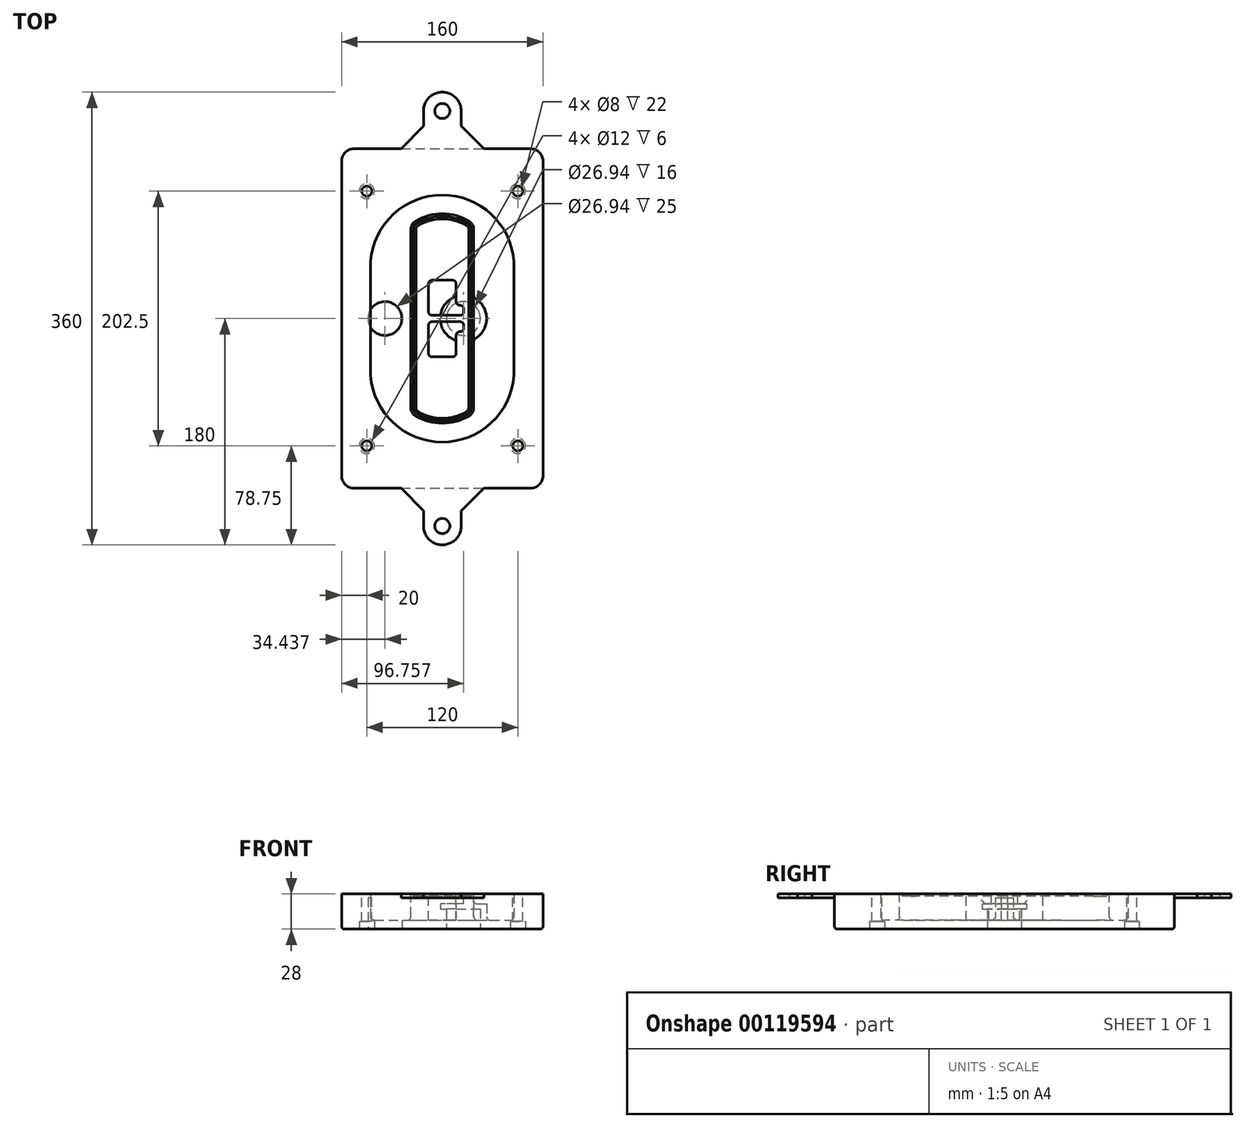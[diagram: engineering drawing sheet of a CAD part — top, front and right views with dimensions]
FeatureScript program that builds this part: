
annotation { "Feature Type Name" : "Feature", "Feature Type Description" : "" }
export const myFeature = defineFeature(function(context is Context, id is Id, definition is map)
    precondition{}
    {
        {
            var Q0;
            Q0=qCreatedBy(makeId("Top.planeOp"),FACE);
            var sketch = newSketch(context, id + "F0", { "sketchPlane" : qUnion([Q0])});
            skPoint(sketch, "E0.rect.middle", {"position": v(0, 0) * mm});
            skLineSegment(sketch, "E1.bottom", {"start": v(-70, -135) * mm, "end": v(70, -135) * mm});
            skLineSegment(sketch, "E1.top", {"start": v(-70, 135) * mm, "end": v(70, 135) * mm});
            skLineSegment(sketch, "E1.left", {"start": v(-80, -125) * mm, "end": v(-80, 125) * mm});
            skLineSegment(sketch, "E1.right", {"start": v(80, -125) * mm, "end": v(80, 125) * mm});
            skLineSegment(sketch, "E2", {"start": v(-80, 135) * mm, "end": v(80, -135) * mm, "construction": true});
            skLineSegment(sketch, "E3", {"start": v(80, 135) * mm, "end": v(-80, -135) * mm, "construction": true});
            skCircle(sketch, "E4", {"center": v(-60, 101.25) * mm, "radius": 4 * mm});
            skCircle(sketch, "E5", {"center": v(60, 101.25) * mm, "radius": 4 * mm});
            skCircle(sketch, "E6", {"center": v(60, -101.25) * mm, "radius": 4 * mm});
            skCircle(sketch, "E7", {"center": v(-60, -101.25) * mm, "radius": 4 * mm});
            skLineSegment(sketch, "E8", {"start": v(-60, 101.25) * mm, "end": v(60, 101.25) * mm, "construction": true});
            skLineSegment(sketch, "E9", {"start": v(60, 101.25) * mm, "end": v(60, -101.25) * mm, "construction": true});
            skLineSegment(sketch, "E10", {"start": v(60, -101.25) * mm, "end": v(-60, -101.25) * mm, "construction": true});
            skLineSegment(sketch, "E11", {"start": v(-60, -101.25) * mm, "end": v(-60, 101.25) * mm, "construction": true});
            skLineSegment(sketch, "E12", {"start": v(-60, 44.66) * mm, "end": v(-60, -44.66) * mm});
            skLineSegment(sketch, "E13", {"start": v(60, 44.66) * mm, "end": v(60, -44.66) * mm});
            skArc(sketch, "E14", {"start": v(59.98, 45.37) * mm, "mid": v(0, 101.25) * mm, "end": v(-59.98, 45.37) * mm});
            skArc(sketch, "E15", {"start": v(-59.98, -45.37) * mm, "mid": v(0, -101.25) * mm, "end": v(59.98, -45.37) * mm});
            skLineSegment(sketch, "E16", {"start": v(-60, 0) * mm, "end": v(60, 0) * mm, "construction": true});
            skPoint(sketch, "E17.visualSharp", {"position": v(-60, -45) * mm});
            skArc(sketch, "E17.filletArc", {"start": v(-60, -44.66) * mm, "mid": v(-60, -45.02) * mm, "end": v(-59.98, -45.37) * mm});
            skPoint(sketch, "E18.visualSharp", {"position": v(-60, 45) * mm});
            skArc(sketch, "E18.filletArc", {"start": v(-59.98, 45.37) * mm, "mid": v(-60, 45.02) * mm, "end": v(-60, 44.66) * mm});
            skPoint(sketch, "E19.visualSharp", {"position": v(60, 45) * mm});
            skArc(sketch, "E19.filletArc", {"start": v(60, 44.66) * mm, "mid": v(60, 45.02) * mm, "end": v(59.98, 45.37) * mm});
            skPoint(sketch, "E20.visualSharp", {"position": v(60, -45) * mm});
            skArc(sketch, "E20.filletArc", {"start": v(59.98, -45.37) * mm, "mid": v(60, -45.02) * mm, "end": v(60, -44.66) * mm});
            skPoint(sketch, "E21.visualSharp", {"position": v(-80, 135) * mm});
            skArc(sketch, "E21.filletArc", {"start": v(-70, 135) * mm, "mid": v(-77.07, 132.07) * mm, "end": v(-80, 125) * mm});
            skPoint(sketch, "E22.visualSharp", {"position": v(80, 135) * mm});
            skArc(sketch, "E22.filletArc", {"start": v(80, 125) * mm, "mid": v(77.07, 132.07) * mm, "end": v(70, 135) * mm});
            skPoint(sketch, "E23.visualSharp", {"position": v(80, -135) * mm});
            skArc(sketch, "E23.filletArc", {"start": v(70, -135) * mm, "mid": v(77.07, -132.07) * mm, "end": v(80, -125) * mm});
            skPoint(sketch, "E24.visualSharp", {"position": v(-80, -135) * mm});
            skArc(sketch, "E24.filletArc", {"start": v(-80, -125) * mm, "mid": v(-77.07, -132.07) * mm, "end": v(-70, -135) * mm});
            skArc(sketch, "E25.0", {"start": v(57, 44.66) * mm, "mid": v(57, 44.9) * mm, "end": v(56.98, 45.16) * mm});
            skLineSegment(sketch, "E25.1", {"start": v(57, 44.66) * mm, "end": v(57, -44.66) * mm});
            skArc(sketch, "E25.2", {"start": v(56.98, -45.16) * mm, "mid": v(57, -44.9) * mm, "end": v(57, -44.66) * mm});
            skArc(sketch, "E25.3", {"start": v(-56.98, -45.16) * mm, "mid": v(0, -98.25) * mm, "end": v(56.98, -45.16) * mm});
            skArc(sketch, "E25.4", {"start": v(-57, -44.66) * mm, "mid": v(-57, -44.9) * mm, "end": v(-56.98, -45.16) * mm});
            skArc(sketch, "E25.5", {"start": v(56.98, 45.16) * mm, "mid": v(0, 98.25) * mm, "end": v(-56.98, 45.16) * mm});
            skLineSegment(sketch, "E25.6", {"start": v(-57, 44.66) * mm, "end": v(-57, -44.66) * mm});
            skArc(sketch, "E25.7", {"start": v(-56.98, 45.16) * mm, "mid": v(-57, 44.9) * mm, "end": v(-57, 44.66) * mm});
            skArc(sketch, "E26.0", {"start": v(-63.97, 45.65) * mm, "mid": v(-64, 45.16) * mm, "end": v(-64, 44.66) * mm});
            skArc(sketch, "E26.1", {"start": v(63.97, 45.65) * mm, "mid": v(0, 105.25) * mm, "end": v(-63.97, 45.65) * mm});
            skArc(sketch, "E26.2", {"start": v(64, 44.66) * mm, "mid": v(64, 45.16) * mm, "end": v(63.97, 45.65) * mm});
            skLineSegment(sketch, "E26.3", {"start": v(64, 44.66) * mm, "end": v(64, -44.66) * mm});
            skArc(sketch, "E26.4", {"start": v(63.97, -45.65) * mm, "mid": v(64, -45.16) * mm, "end": v(64, -44.66) * mm});
            skLineSegment(sketch, "E26.5", {"start": v(-64, 44.66) * mm, "end": v(-64, -44.66) * mm});
            skArc(sketch, "E26.6", {"start": v(-63.97, -45.65) * mm, "mid": v(0, -105.25) * mm, "end": v(63.97, -45.65) * mm});
            skArc(sketch, "E26.7", {"start": v(-64, -44.66) * mm, "mid": v(-64, -45.16) * mm, "end": v(-63.97, -45.65) * mm});
            skSolve(sketch);
        }
        {
            var Q0;
            Q0=makeQuery(id+"F0.imprint","IMPRINT",FACE,{"disambiguationData":[TD([[makeQuery(id+"F0.imprint","IMPRINT",EDGE,{"derivedFrom":sQuery(id+"F0.wireOp",EDGE,"E1.bottom")}),1.0]])]});
            var Q1;
            Q1=makeQuery(id+"F0.imprint","IMPRINT",FACE,{"disambiguationData":[TD([[makeQuery(id+"F0.imprint","IMPRINT",EDGE,{"derivedFrom":sQuery(id+"F0.wireOp",EDGE,"E12")}),1.0]])]});
            var Q2;
            Q2=makeQuery(id+"F0.imprint","IMPRINT",FACE,{"disambiguationData":[TD([[makeQuery(id+"F0.imprint","IMPRINT",EDGE,{"derivedFrom":sQuery(id+"F0.wireOp",EDGE,"E25.0")}),1.0]])]});
            var Q3;
            Q3=makeQuery(id+"F0.imprint","IMPRINT",FACE,{"disambiguationData":[TD([[makeQuery(id+"F0.imprint","IMPRINT",EDGE,{"derivedFrom":sQuery(id+"F0.wireOp",EDGE,"E12")}),-1.0]])]});
            extrude(context, id + "F1", {"entities" : qUnion([Q0, Q1, Q2, Q3]), "oppositeDirection" : true, "depth" : 25 * mm});
        }
        {
            var Q0;
            Q0=makeQuery(id+"F0.imprint","IMPRINT",FACE,{"disambiguationData":[TD([[makeQuery(id+"F0.imprint","IMPRINT",EDGE,{"derivedFrom":sQuery(id+"F0.wireOp",EDGE,"E12")}),1.0]])]});
            extrude(context, id + "F2", {"entities" : qUnion([Q0]), "operationType" : NewBodyOperationType.ADD, "depth" : 3 * mm});
        }
        {
            var Q0;
            Q0=makeQuery(id+"F0.imprint","IMPRINT",FACE,{"disambiguationData":[TD([[makeQuery(id+"F0.imprint","IMPRINT",EDGE,{"derivedFrom":sQuery(id+"F0.wireOp",EDGE,"E25.0")}),1.0]])]});
            extrude(context, id + "F3", {"entities" : qUnion([Q0]), "operationType" : NewBodyOperationType.REMOVE, "oppositeDirection" : true, "depth" : 18 * mm});
        }
        {
            var Q0;
            Q0=makeQuery(id+"F2.opExtrude","CAP_FACE",FACE,{"disambiguationData":[OSD([sQuery(id+"F0.wireOp",EDGE,"E12"),sQuery(id+"F0.wireOp",EDGE,"E13"),sQuery(id+"F0.wireOp",EDGE,"E14"),sQuery(id+"F0.wireOp",EDGE,"E15"),sQuery(id+"F0.wireOp",EDGE,"E17.filletArc"),sQuery(id+"F0.wireOp",EDGE,"E18.filletArc"),sQuery(id+"F0.wireOp",EDGE,"E19.filletArc"),sQuery(id+"F0.wireOp",EDGE,"E20.filletArc"),sQuery(id+"F0.wireOp",EDGE,"E25.0"),sQuery(id+"F0.wireOp",EDGE,"E25.1"),sQuery(id+"F0.wireOp",EDGE,"E25.2"),sQuery(id+"F0.wireOp",EDGE,"E25.3"),sQuery(id+"F0.wireOp",EDGE,"E25.4"),sQuery(id+"F0.wireOp",EDGE,"E25.5"),sQuery(id+"F0.wireOp",EDGE,"E25.6"),sQuery(id+"F0.wireOp",EDGE,"E25.7")])],"isStart":false});
            var sketch = newSketch(context, id + "F4", { "sketchPlane" : qUnion([Q0])});
            skArc(sketch, "E27.0", {"start": v(-20.99, -77.65) * mm, "mid": v(0, -83.25) * mm, "end": v(20.99, -77.65) * mm});
            skArc(sketch, "E28.0", {"start": v(20.99, 77.65) * mm, "mid": v(0, 83.25) * mm, "end": v(-20.99, 77.65) * mm});
            skLineSegment(sketch, "E29", {"start": v(-25, 70.71) * mm, "end": v(-25, -70.71) * mm});
            skLineSegment(sketch, "E30", {"start": v(25, 70.71) * mm, "end": v(25, -70.71) * mm});
            skLineSegment(sketch, "E31", {"start": v(-25, 75.03) * mm, "end": v(25, 75.03) * mm, "construction": true});
            skLineSegment(sketch, "E32", {"start": v(-25, -75.03) * mm, "end": v(25, -75.03) * mm, "construction": true});
            skPoint(sketch, "E33.visualSharp", {"position": v(-25, 75.03) * mm});
            skArc(sketch, "E33.filletArc", {"start": v(-20.99, 77.65) * mm, "mid": v(-23.92, 74.72) * mm, "end": v(-25, 70.71) * mm});
            skPoint(sketch, "E34.visualSharp", {"position": v(25, 75.03) * mm});
            skArc(sketch, "E34.filletArc", {"start": v(25, 70.71) * mm, "mid": v(23.92, 74.72) * mm, "end": v(20.99, 77.65) * mm});
            skPoint(sketch, "E35.visualSharp", {"position": v(25, -75.03) * mm});
            skArc(sketch, "E35.filletArc", {"start": v(20.99, -77.65) * mm, "mid": v(23.92, -74.72) * mm, "end": v(25, -70.71) * mm});
            skPoint(sketch, "E36.visualSharp", {"position": v(-25, -75.03) * mm});
            skArc(sketch, "E36.filletArc", {"start": v(-25, -70.71) * mm, "mid": v(-23.92, -74.72) * mm, "end": v(-20.99, -77.65) * mm});
            skArc(sketch, "E37.0", {"start": v(56.98, 45.16) * mm, "mid": v(0, 98.25) * mm, "end": v(-56.98, 45.16) * mm});
            skArc(sketch, "E37.1", {"start": v(-56.98, 45.16) * mm, "mid": v(-57, 44.9) * mm, "end": v(-57, 44.66) * mm});
            skLineSegment(sketch, "E37.2", {"start": v(-57, 44.66) * mm, "end": v(-57, -44.66) * mm});
            skArc(sketch, "E37.3", {"start": v(-57, -44.66) * mm, "mid": v(-57, -44.9) * mm, "end": v(-56.98, -45.16) * mm});
            skArc(sketch, "E37.4", {"start": v(-56.98, -45.16) * mm, "mid": v(0, -98.25) * mm, "end": v(56.98, -45.16) * mm});
            skArc(sketch, "E37.5", {"start": v(56.98, -45.16) * mm, "mid": v(57, -44.9) * mm, "end": v(57, -44.66) * mm});
            skLineSegment(sketch, "E37.6", {"start": v(57, 44.66) * mm, "end": v(57, -44.66) * mm});
            skArc(sketch, "E37.7", {"start": v(57, 44.66) * mm, "mid": v(57, 44.9) * mm, "end": v(56.98, 45.16) * mm});
            skLineSegment(sketch, "E38.0", {"start": v(23, 70.71) * mm, "end": v(23, -70.71) * mm});
            skArc(sketch, "E38.1", {"start": v(19.99, -75.92) * mm, "mid": v(22.2, -73.72) * mm, "end": v(23, -70.71) * mm});
            skArc(sketch, "E38.2", {"start": v(-19.99, -75.92) * mm, "mid": v(0, -81.25) * mm, "end": v(19.99, -75.92) * mm});
            skArc(sketch, "E38.3", {"start": v(-23, -70.71) * mm, "mid": v(-22.2, -73.72) * mm, "end": v(-19.99, -75.92) * mm});
            skLineSegment(sketch, "E38.4", {"start": v(-23, 70.71) * mm, "end": v(-23, -70.71) * mm});
            skArc(sketch, "E38.5", {"start": v(23, 70.71) * mm, "mid": v(22.2, 73.72) * mm, "end": v(19.99, 75.92) * mm});
            skArc(sketch, "E38.6", {"start": v(-19.99, 75.92) * mm, "mid": v(-22.2, 73.72) * mm, "end": v(-23, 70.71) * mm});
            skArc(sketch, "E38.7", {"start": v(19.99, 75.92) * mm, "mid": v(0, 81.25) * mm, "end": v(-19.99, 75.92) * mm});
            skArc(sketch, "E39.0", {"start": v(21, 70.71) * mm, "mid": v(20.46, 72.72) * mm, "end": v(19, 74.18) * mm});
            skLineSegment(sketch, "E39.1", {"start": v(21, 70.71) * mm, "end": v(21, -70.71) * mm});
            skArc(sketch, "E39.2", {"start": v(19, -74.18) * mm, "mid": v(20.46, -72.72) * mm, "end": v(21, -70.71) * mm});
            skArc(sketch, "E39.3", {"start": v(-19, -74.18) * mm, "mid": v(0, -79.25) * mm, "end": v(19, -74.18) * mm});
            skArc(sketch, "E39.4", {"start": v(-21, -70.71) * mm, "mid": v(-20.46, -72.72) * mm, "end": v(-19, -74.18) * mm});
            skArc(sketch, "E39.5", {"start": v(19, 74.18) * mm, "mid": v(0, 79.25) * mm, "end": v(-19, 74.18) * mm});
            skLineSegment(sketch, "E39.6", {"start": v(-21, 70.71) * mm, "end": v(-21, -70.71) * mm});
            skArc(sketch, "E39.7", {"start": v(-19, 74.18) * mm, "mid": v(-20.46, 72.72) * mm, "end": v(-21, 70.71) * mm});
            skLineSegment(sketch, "E40", {"start": v(-25, 0) * mm, "end": v(25, 0) * mm, "construction": true});
            skLineSegment(sketch, "E41", {"start": v(-11, 5.5) * mm, "end": v(-11, 27.5) * mm});
            skLineSegment(sketch, "E42", {"start": v(-8, 30.5) * mm, "end": v(8, 30.5) * mm});
            skLineSegment(sketch, "E43", {"start": v(11, 27.5) * mm, "end": v(11, 13.5) * mm});
            skLineSegment(sketch, "E44", {"start": v(14, 10.5) * mm, "end": v(14, 10.5) * mm});
            skLineSegment(sketch, "E45", {"start": v(17, 7.5) * mm, "end": v(17, 5.5) * mm});
            skLineSegment(sketch, "E46", {"start": v(14, 2.5) * mm, "end": v(-8, 2.5) * mm});
            skPoint(sketch, "E47.visualSharp", {"position": v(-11, 30.5) * mm});
            skArc(sketch, "E47.filletArc", {"start": v(-8, 30.5) * mm, "mid": v(-10.12, 29.62) * mm, "end": v(-11, 27.5) * mm});
            skPoint(sketch, "E48.visualSharp", {"position": v(11, 30.5) * mm});
            skArc(sketch, "E48.filletArc", {"start": v(11, 27.5) * mm, "mid": v(10.12, 29.62) * mm, "end": v(8, 30.5) * mm});
            skPoint(sketch, "E49.visualSharp", {"position": v(11, 10.5) * mm});
            skArc(sketch, "E49.filletArc", {"start": v(11, 13.5) * mm, "mid": v(11.88, 11.38) * mm, "end": v(14, 10.5) * mm});
            skPoint(sketch, "E50.visualSharp", {"position": v(17, 10.5) * mm});
            skArc(sketch, "E50.filletArc", {"start": v(17, 7.5) * mm, "mid": v(16.12, 9.62) * mm, "end": v(14, 10.5) * mm});
            skPoint(sketch, "E51.visualSharp", {"position": v(17, 2.5) * mm});
            skArc(sketch, "E51.filletArc", {"start": v(14, 2.5) * mm, "mid": v(16.12, 3.38) * mm, "end": v(17, 5.5) * mm});
            skPoint(sketch, "E52.visualSharp", {"position": v(-11, 2.5) * mm});
            skArc(sketch, "E52.filletArc", {"start": v(-11, 5.5) * mm, "mid": v(-10.12, 3.38) * mm, "end": v(-8, 2.5) * mm});
            skLineSegment(sketch, "E53.0.MirrorCS", {"start": v(14, -2.5) * mm, "end": v(-8, -2.5) * mm});
            skArc(sketch, "E54.0.MirrorCS", {"start": v(-11, -5.5) * mm, "mid": v(-10.12, -3.38) * mm, "end": v(-8, -2.5) * mm});
            skLineSegment(sketch, "E55.0.MirrorCS", {"start": v(-11, -5.5) * mm, "end": v(-11, -27.5) * mm});
            skArc(sketch, "E56.0.MirrorCS", {"start": v(-8, -30.5) * mm, "mid": v(-10.12, -29.62) * mm, "end": v(-11, -27.5) * mm});
            skLineSegment(sketch, "E57.0.MirrorCS", {"start": v(-8, -30.5) * mm, "end": v(8, -30.5) * mm});
            skArc(sketch, "E58.0.MirrorCS", {"start": v(11, -27.5) * mm, "mid": v(10.12, -29.62) * mm, "end": v(8, -30.5) * mm});
            skLineSegment(sketch, "E59.0.MirrorCS", {"start": v(11, -27.5) * mm, "end": v(11, -13.5) * mm});
            skArc(sketch, "E60.0.MirrorCS", {"start": v(11, -13.5) * mm, "mid": v(11.88, -11.38) * mm, "end": v(14, -10.5) * mm});
            skArc(sketch, "E61.0.MirrorCS", {"start": v(17, -7.5) * mm, "mid": v(16.12, -9.62) * mm, "end": v(14, -10.5) * mm});
            skLineSegment(sketch, "E62.0.MirrorCS", {"start": v(17, -7.5) * mm, "end": v(17, -5.5) * mm});
            skArc(sketch, "E63.0.MirrorCS", {"start": v(14, -2.5) * mm, "mid": v(16.12, -3.38) * mm, "end": v(17, -5.5) * mm});
            skSolve(sketch);
        }
        {
            var Q0;
            Q0=makeQuery(id+"F4.imprint","IMPRINT",FACE,{"disambiguationData":[TD([[makeQuery(id+"F4.imprint","IMPRINT",EDGE,{"derivedFrom":sQuery(id+"F4.wireOp",EDGE,"E27.0")}),1.0]])]});
            var Q1;
            Q1=makeQuery(id+"F4.imprint","IMPRINT",FACE,{"disambiguationData":[TD([[makeQuery(id+"F4.imprint","IMPRINT",EDGE,{"derivedFrom":sQuery(id+"F4.wireOp",EDGE,"E38.0")}),-1.0]])]});
            var Q2;
            Q2=makeQuery(id+"F4.imprint","IMPRINT",FACE,{"disambiguationData":[TD([[makeQuery(id+"F4.imprint","IMPRINT",EDGE,{"derivedFrom":sQuery(id+"F4.wireOp",EDGE,"E39.0")}),1.0]])]});
            extrude(context, id + "F5", {"entities" : qUnion([Q0, Q1, Q2]), "operationType" : NewBodyOperationType.ADD, "endBound" : BoundingType.UP_TO_NEXT, "oppositeDirection" : true, "depth" : 25 * mm});
        }
        {
            var Q0;
            Q0=makeQuery(id+"F4.imprint","IMPRINT",FACE,{"disambiguationData":[TD([[makeQuery(id+"F4.imprint","IMPRINT",EDGE,{"derivedFrom":sQuery(id+"F4.wireOp",EDGE,"E38.0")}),-1.0]])]});
            extrude(context, id + "F6", {"entities" : qUnion([Q0]), "operationType" : NewBodyOperationType.REMOVE, "oppositeDirection" : true, "depth" : 2 * mm});
        }
        {
            var Q0;
            Q0=makeQuery(id+"F1.opExtrude","CAP_FACE",FACE,{"disambiguationData":[OSD([sQuery(id+"F0.wireOp",EDGE,"E1.bottom"),sQuery(id+"F0.wireOp",EDGE,"E1.top"),sQuery(id+"F0.wireOp",EDGE,"E1.left"),sQuery(id+"F0.wireOp",EDGE,"E1.right"),sQuery(id+"F0.wireOp",EDGE,"E4"),sQuery(id+"F0.wireOp",EDGE,"E5"),sQuery(id+"F0.wireOp",EDGE,"E6"),sQuery(id+"F0.wireOp",EDGE,"E7"),sQuery(id+"F0.wireOp",EDGE,"E21.filletArc"),sQuery(id+"F0.wireOp",EDGE,"E22.filletArc"),sQuery(id+"F0.wireOp",EDGE,"E23.filletArc"),sQuery(id+"F0.wireOp",EDGE,"E24.filletArc")])],"isStart":false});
            var sketch = newSketch(context, id + "F7", { "sketchPlane" : qUnion([Q0])});
            skCircle(sketch, "E64", {"center": v(16.76, 0) * mm, "radius": 13.47 * mm});
            skCircle(sketch, "E65", {"center": v(-45.56, 0) * mm, "radius": 13.47 * mm});
            skLineSegment(sketch, "E66", {"start": v(80, 0) * mm, "end": v(-80, 0) * mm});
            skCircle(sketch, "E67", {"center": v(16.76, 0) * mm, "radius": 18.47 * mm});
            skCircle(sketch, "E68", {"center": v(60, -101.25) * mm, "radius": 6 * mm});
            skCircle(sketch, "E69", {"center": v(-60, -101.25) * mm, "radius": 6 * mm});
            skCircle(sketch, "E70", {"center": v(-60, 101.25) * mm, "radius": 6 * mm});
            skCircle(sketch, "E71", {"center": v(60, 101.25) * mm, "radius": 6 * mm});
            skSolve(sketch);
        }
        {
            var Q0;
            {var subQ1=sQuery(id+"F7.wireOp",EDGE,"E66");var subQ4=sQuery(id+"F7.wireOp",EDGE,"E64");var subQ6=makeQuery(id+"F7.imprint","INTERSECT",VERTEX,{"disambiguationData":[OD(0.0)],"derivedFrom":[subQ4,subQ1]});Q0=makeQuery(id+"F7.imprint","IMPRINT",FACE,{"disambiguationData":[TD([[makeQuery(id+"F7.imprint","IMPRINT",EDGE,{"disambiguationData":[TD([[subQ6,-1.0]])],"derivedFrom":subQ4}),-1.0]])]});}
            var Q1;
            {var subQ0=sQuery(id+"F7.wireOp",EDGE,"E66");var subQ1=sQuery(id+"F7.wireOp",EDGE,"E64");var subQ3=makeQuery(id+"F7.imprint","INTERSECT",VERTEX,{"disambiguationData":[OD(0.0)],"derivedFrom":[subQ1,subQ0]});Q1=makeQuery(id+"F7.imprint","IMPRINT",FACE,{"disambiguationData":[TD([[makeQuery(id+"F7.imprint","IMPRINT",EDGE,{"disambiguationData":[TD([[subQ3,-1.0]])],"derivedFrom":subQ1}),1.0]])]});}
            var Q2;
            {var subQ0=sQuery(id+"F7.wireOp",EDGE,"E66");var subQ1=sQuery(id+"F7.wireOp",EDGE,"E64");var subQ3=makeQuery(id+"F7.imprint","INTERSECT",VERTEX,{"disambiguationData":[OD(0.0)],"derivedFrom":[subQ1,subQ0]});Q2=makeQuery(id+"F7.imprint","IMPRINT",FACE,{"disambiguationData":[TD([[makeQuery(id+"F7.imprint","IMPRINT",EDGE,{"disambiguationData":[TD([[subQ3,1.0]])],"derivedFrom":subQ1}),1.0]])]});}
            var Q3;
            {var subQ1=sQuery(id+"F7.wireOp",EDGE,"E66");var subQ4=sQuery(id+"F7.wireOp",EDGE,"E64");var subQ6=makeQuery(id+"F7.imprint","INTERSECT",VERTEX,{"disambiguationData":[OD(0.0)],"derivedFrom":[subQ4,subQ1]});Q3=makeQuery(id+"F7.imprint","IMPRINT",FACE,{"disambiguationData":[TD([[makeQuery(id+"F7.imprint","IMPRINT",EDGE,{"disambiguationData":[TD([[subQ6,1.0]])],"derivedFrom":subQ4}),-1.0]])]});}
            extrude(context, id + "F8", {"entities" : qUnion([Q0, Q1, Q2, Q3]), "operationType" : NewBodyOperationType.ADD, "oppositeDirection" : true, "depth" : 20 * mm});
        }
        {
            var Q0;
            {var subQ0=sQuery(id+"F7.wireOp",EDGE,"E66");var subQ1=sQuery(id+"F7.wireOp",EDGE,"E64");var subQ3=makeQuery(id+"F7.imprint","INTERSECT",VERTEX,{"disambiguationData":[OD(0.0)],"derivedFrom":[subQ1,subQ0]});Q0=makeQuery(id+"F7.imprint","IMPRINT",FACE,{"disambiguationData":[TD([[makeQuery(id+"F7.imprint","IMPRINT",EDGE,{"disambiguationData":[TD([[subQ3,-1.0]])],"derivedFrom":subQ1}),1.0]])]});}
            var Q1;
            {var subQ0=sQuery(id+"F7.wireOp",EDGE,"E66");var subQ1=sQuery(id+"F7.wireOp",EDGE,"E64");var subQ3=makeQuery(id+"F7.imprint","INTERSECT",VERTEX,{"disambiguationData":[OD(0.0)],"derivedFrom":[subQ1,subQ0]});Q1=makeQuery(id+"F7.imprint","IMPRINT",FACE,{"disambiguationData":[TD([[makeQuery(id+"F7.imprint","IMPRINT",EDGE,{"disambiguationData":[TD([[subQ3,1.0]])],"derivedFrom":subQ1}),1.0]])]});}
            extrude(context, id + "F9", {"entities" : qUnion([Q0, Q1]), "operationType" : NewBodyOperationType.REMOVE, "oppositeDirection" : true, "depth" : 16 * mm});
        }
        {
            var Q0;
            {var subQ0=sQuery(id+"F7.wireOp",EDGE,"E66");var subQ1=sQuery(id+"F7.wireOp",EDGE,"E65");var subQ3=makeQuery(id+"F7.imprint","INTERSECT",VERTEX,{"disambiguationData":[OD(0.0)],"derivedFrom":[subQ1,subQ0]});Q0=makeQuery(id+"F7.imprint","IMPRINT",FACE,{"disambiguationData":[TD([[makeQuery(id+"F7.imprint","IMPRINT",EDGE,{"disambiguationData":[TD([[subQ3,-1.0]])],"derivedFrom":subQ1}),1.0]])]});}
            var Q1;
            {var subQ0=sQuery(id+"F7.wireOp",EDGE,"E66");var subQ1=sQuery(id+"F7.wireOp",EDGE,"E65");var subQ3=makeQuery(id+"F7.imprint","INTERSECT",VERTEX,{"disambiguationData":[OD(0.0)],"derivedFrom":[subQ1,subQ0]});Q1=makeQuery(id+"F7.imprint","IMPRINT",FACE,{"disambiguationData":[TD([[makeQuery(id+"F7.imprint","IMPRINT",EDGE,{"disambiguationData":[TD([[subQ3,1.0]])],"derivedFrom":subQ1}),1.0]])]});}
            extrude(context, id + "F10", {"entities" : qUnion([Q0, Q1]), "operationType" : NewBodyOperationType.REMOVE, "oppositeDirection" : true, "depth" : 25 * mm});
        }
        {
            var Q0;
            Q0=makeQuery(id+"F7.imprint","IMPRINT",FACE,{"disambiguationData":[TD([[makeQuery(id+"F7.imprint","IMPRINT",EDGE,{"derivedFrom":sQuery(id+"F7.wireOp",EDGE,"E68")}),1.0]])]});
            var Q1;
            Q1=makeQuery(id+"F7.imprint","IMPRINT",FACE,{"disambiguationData":[TD([[makeQuery(id+"F7.imprint","IMPRINT",EDGE,{"derivedFrom":makeQuery(id+"F1.opExtrude","CAP_EDGE",EDGE,{"disambiguationData":[OSD([sQuery(id+"F0.wireOp",EDGE,"E5")])],"isStart":false})}),-1.0]])]});
            var Q2;
            Q2=makeQuery(id+"F7.imprint","IMPRINT",FACE,{"disambiguationData":[TD([[makeQuery(id+"F7.imprint","IMPRINT",EDGE,{"derivedFrom":sQuery(id+"F7.wireOp",EDGE,"E69")}),1.0]])]});
            var Q3;
            Q3=makeQuery(id+"F7.imprint","IMPRINT",FACE,{"disambiguationData":[TD([[makeQuery(id+"F7.imprint","IMPRINT",EDGE,{"derivedFrom":makeQuery(id+"F1.opExtrude","CAP_EDGE",EDGE,{"disambiguationData":[OSD([sQuery(id+"F0.wireOp",EDGE,"E4")])],"isStart":false})}),-1.0]])]});
            var Q4;
            Q4=makeQuery(id+"F7.imprint","IMPRINT",FACE,{"disambiguationData":[TD([[makeQuery(id+"F7.imprint","IMPRINT",EDGE,{"derivedFrom":sQuery(id+"F7.wireOp",EDGE,"E70")}),1.0]])]});
            var Q5;
            Q5=makeQuery(id+"F7.imprint","IMPRINT",FACE,{"disambiguationData":[TD([[makeQuery(id+"F7.imprint","IMPRINT",EDGE,{"derivedFrom":makeQuery(id+"F1.opExtrude","CAP_EDGE",EDGE,{"disambiguationData":[OSD([sQuery(id+"F0.wireOp",EDGE,"E7")])],"isStart":false})}),-1.0]])]});
            var Q6;
            Q6=makeQuery(id+"F7.imprint","IMPRINT",FACE,{"disambiguationData":[TD([[makeQuery(id+"F7.imprint","IMPRINT",EDGE,{"derivedFrom":sQuery(id+"F7.wireOp",EDGE,"E71")}),1.0]])]});
            var Q7;
            Q7=makeQuery(id+"F7.imprint","IMPRINT",FACE,{"disambiguationData":[TD([[makeQuery(id+"F7.imprint","IMPRINT",EDGE,{"derivedFrom":makeQuery(id+"F1.opExtrude","CAP_EDGE",EDGE,{"disambiguationData":[OSD([sQuery(id+"F0.wireOp",EDGE,"E6")])],"isStart":false})}),-1.0]])]});
            extrude(context, id + "F11", {"entities" : qUnion([Q0, Q1, Q2, Q3, Q4, Q5, Q6, Q7]), "operationType" : NewBodyOperationType.REMOVE, "oppositeDirection" : true, "depth" : 6 * mm});
        }
        {
            var Q0;
            Q0=makeQuery(id+"F9.boolean.opBoolean","COPY",FACE,{"derivedFrom":makeQuery(id+"F9.opExtrude","CAP_FACE",FACE,{"disambiguationData":[OSD([sQuery(id+"F7.wireOp",EDGE,"E64")])],"isStart":false})});
            var sketch = newSketch(context, id + "F12", { "sketchPlane" : qUnion([Q0])});
            skArc(sketch, "E72.0", {"start": v(11, 17.55) * mm, "mid": v(2.57, 11.82) * mm, "end": v(-1.54, 2.5) * mm});
            skArc(sketch, "E72.1", {"start": v(-1.54, -2.5) * mm, "mid": v(2.57, -11.82) * mm, "end": v(11, -17.55) * mm});
            skLineSegment(sketch, "E73", {"start": v(-1.54, -2.5) * mm, "end": v(14, -2.5) * mm});
            skLineSegment(sketch, "E74.0", {"start": v(14, 2.5) * mm, "end": v(-1.54, 2.5) * mm});
            skArc(sketch, "E74.1", {"start": v(14, 2.5) * mm, "mid": v(16.12, 3.38) * mm, "end": v(17, 5.5) * mm});
            skLineSegment(sketch, "E74.2", {"start": v(17, 7.5) * mm, "end": v(17, 5.5) * mm});
            skArc(sketch, "E74.3", {"start": v(17, 7.5) * mm, "mid": v(16.12, 9.62) * mm, "end": v(14, 10.5) * mm});
            skArc(sketch, "E74.4", {"start": v(11, 13.5) * mm, "mid": v(11.88, 11.38) * mm, "end": v(14, 10.5) * mm});
            skLineSegment(sketch, "E74.5", {"start": v(11, 17.55) * mm, "end": v(11, 13.5) * mm});
            skLineSegment(sketch, "E74.7", {"start": v(14, -2.5) * mm, "end": v(-1.54, -2.5) * mm});
            skArc(sketch, "E74.8", {"start": v(14, -2.5) * mm, "mid": v(16.12, -3.38) * mm, "end": v(17, -5.5) * mm});
            skLineSegment(sketch, "E74.9", {"start": v(17, -7.5) * mm, "end": v(17, -5.5) * mm});
            skArc(sketch, "E74.10", {"start": v(17, -7.5) * mm, "mid": v(16.12, -9.62) * mm, "end": v(14, -10.5) * mm});
            skArc(sketch, "E74.11", {"start": v(11, -13.5) * mm, "mid": v(11.88, -11.38) * mm, "end": v(14, -10.5) * mm});
            skLineSegment(sketch, "E74.12", {"start": v(11, -17.55) * mm, "end": v(11, -13.5) * mm});
            skPoint(sketch, "E75.orphan", {"position": v(11, -27.5) * mm});
            skPoint(sketch, "E76.orphan", {"position": v(-8, -2.5) * mm});
            skPoint(sketch, "E77.orphan", {"position": v(-8, 2.5) * mm});
            skPoint(sketch, "E78.orphan", {"position": v(11, 27.5) * mm});
            skSolve(sketch);
        }
        {
            var Q0;
            {var subQ7=sQuery(id+"F12.wireOp",EDGE,"E72.0");var subQ14=sQuery(id+"F12.wireOp",EDGE,"E72.1");var subQ16=sQuery(id+"F12.wireOp",EDGE,"E74.1");var subQ18=sQuery(id+"F12.wireOp",EDGE,"E74.8");Q0=qUnion([makeQuery(id+"F12.imprint","IMPRINT",FACE,{"disambiguationData":[TD([[makeQuery(id+"F12.imprint","IMPRINT",EDGE,{"derivedFrom":subQ7}),1.0]])]}),makeQuery(id+"F12.imprint","IMPRINT",FACE,{"disambiguationData":[TD([[makeQuery(id+"F12.imprint","IMPRINT",EDGE,{"derivedFrom":subQ14}),1.0]])]}),makeQuery(id+"F12.imprint","IMPRINT",FACE,{"disambiguationData":[TD([[makeQuery(id+"F12.imprint","IMPRINT",EDGE,{"derivedFrom":subQ16}),1.0]])]}),makeQuery(id+"F12.imprint","IMPRINT",FACE,{"disambiguationData":[TD([[makeQuery(id+"F12.imprint","IMPRINT",EDGE,{"derivedFrom":subQ18}),-1.0]])]})]);}
            var Q1;
            Q1=makeQuery(id+"F5.boolean.opBoolean","SPLIT",FACE,{"disambiguationData":[TD([makeQuery(id+"F5.opExtrude","SWEPT_FACE",FACE,{"disambiguationData":[OSD([sQuery(id+"F4.wireOp",EDGE,"E41")])]})])],"derivedFrom":makeQuery(id+"F3.boolean.opBoolean","COPY",FACE,{"derivedFrom":makeQuery(id+"F3.opExtrude","CAP_FACE",FACE,{"disambiguationData":[OSD([sQuery(id+"F0.wireOp",EDGE,"E25.0"),sQuery(id+"F0.wireOp",EDGE,"E25.1"),sQuery(id+"F0.wireOp",EDGE,"E25.2"),sQuery(id+"F0.wireOp",EDGE,"E25.3"),sQuery(id+"F0.wireOp",EDGE,"E25.4"),sQuery(id+"F0.wireOp",EDGE,"E25.5"),sQuery(id+"F0.wireOp",EDGE,"E25.6"),sQuery(id+"F0.wireOp",EDGE,"E25.7")])],"isStart":false})})});
            extrude(context, id + "F13", {"entities" : qUnion([Q0]), "operationType" : NewBodyOperationType.REMOVE, "endBound" : BoundingType.UP_TO_SURFACE, "endBoundEntityFace" : qUnion([Q1]), "depth" : 25 * mm});
        }
        {
            var Q0;
            Q0=makeQuery(id+"F3.boolean.opBoolean","COPY",EDGE,{"derivedFrom":makeQuery(id+"F3.opExtrude","CAP_EDGE",EDGE,{"disambiguationData":[OSD([sQuery(id+"F0.wireOp",EDGE,"E25.6")])],"isStart":false})});
            var Q1;
            Q1=makeQuery(id+"F8.boolean.opBoolean","INTERSECT",EDGE,{"derivedFrom":[makeQuery(id+"F5.opExtrude","SWEPT_FACE",FACE,{"disambiguationData":[OSD([sQuery(id+"F4.wireOp",EDGE,"E30")])]}),makeQuery(id+"F8.opExtrude","CAP_FACE",FACE,{"disambiguationData":[OSD([sQuery(id+"F7.wireOp",EDGE,"E67")])],"isStart":false})]});
            var Q2;
            Q2=makeQuery(id+"F8.boolean.opBoolean","INTERSECT",EDGE,{"disambiguationData":[OD(1.0)],"derivedFrom":[makeQuery(id+"F5.opExtrude","SWEPT_FACE",FACE,{"disambiguationData":[OSD([sQuery(id+"F4.wireOp",EDGE,"E30")])]}),makeQuery(id+"F8.opExtrude","SWEPT_FACE",FACE,{"disambiguationData":[OSD([sQuery(id+"F7.wireOp",EDGE,"E67")])]})]});
            var Q3;
            {var subQ0=sQuery(id+"F4.wireOp",EDGE,"E30");Q3=makeQuery(id+"F8.boolean.opBoolean","SPLIT",EDGE,{"disambiguationData":[TD([makeQuery(id+"F5.opExtrude","SWEPT_FACE",FACE,{"disambiguationData":[OSD([sQuery(id+"F4.wireOp",EDGE,"E35.filletArc")])]})])],"derivedFrom":makeQuery(id+"F5.opExtrude","CAP_EDGE",EDGE,{"disambiguationData":[OSD([subQ0])],"isStart":false})});}
            var Q4;
            {var subQ0=sQuery(id+"F0.wireOp",EDGE,"E25.7");var subQ1=sQuery(id+"F0.wireOp",EDGE,"E25.1");var subQ2=sQuery(id+"F0.wireOp",EDGE,"E25.6");var subQ3=sQuery(id+"F0.wireOp",EDGE,"E25.5");var subQ4=sQuery(id+"F0.wireOp",EDGE,"E25.4");var subQ5=sQuery(id+"F0.wireOp",EDGE,"E25.0");var subQ6=sQuery(id+"F0.wireOp",EDGE,"E25.2");var subQ7=sQuery(id+"F0.wireOp",EDGE,"E25.3");Q4=makeQuery(id+"F8.boolean.opBoolean","INTERSECT",EDGE,{"derivedFrom":[makeQuery(id+"F5.boolean.opBoolean","SPLIT",FACE,{"disambiguationData":[TD([makeQuery(id+"F2.opExtrude","SWEPT_FACE",FACE,{"disambiguationData":[OSD([subQ5])]})])],"derivedFrom":makeQuery(id+"F3.boolean.opBoolean","COPY",FACE,{"derivedFrom":makeQuery(id+"F3.opExtrude","CAP_FACE",FACE,{"disambiguationData":[OSD([subQ5,subQ1,subQ6,subQ7,subQ4,subQ3,subQ2,subQ0])],"isStart":false})})}),makeQuery(id+"F8.opExtrude","SWEPT_FACE",FACE,{"disambiguationData":[OSD([sQuery(id+"F7.wireOp",EDGE,"E67")])]})]});}
            var Q5;
            Q5=makeQuery(id+"F8.boolean.opBoolean","INTERSECT",EDGE,{"disambiguationData":[OD(0.0)],"derivedFrom":[makeQuery(id+"F5.opExtrude","SWEPT_FACE",FACE,{"disambiguationData":[OSD([sQuery(id+"F4.wireOp",EDGE,"E30")])]}),makeQuery(id+"F8.opExtrude","SWEPT_FACE",FACE,{"disambiguationData":[OSD([sQuery(id+"F7.wireOp",EDGE,"E67")])]})]});
            fillet(context, id + "F14", {"entities" : qUnion([Q0, Q1, Q2, Q3, Q4, Q5]), "radius" : 3 * mm, "tangentPropagation" : true, "allowEdgeOverflow" : false});
        }
        {
            var Q0;
            Q0=makeQuery(id+"F1.opExtrude","CAP_EDGE",EDGE,{"disambiguationData":[OSD([sQuery(id+"F0.wireOp",EDGE,"E1.bottom")])],"isStart":false});
            fillet(context, id + "F15", {"entities" : qUnion([Q0]), "radius" : 2 * mm, "tangentPropagation" : true, "allowEdgeOverflow" : false});
        }
        {
            var Q0;
            {var subQ0=sQuery(id+"F0.wireOp",EDGE,"E22.filletArc");var subQ1=sQuery(id+"F0.wireOp",EDGE,"E7");var subQ2=sQuery(id+"F0.wireOp",EDGE,"E6");var subQ3=sQuery(id+"F0.wireOp",EDGE,"E5");var subQ4=sQuery(id+"F0.wireOp",EDGE,"E4");var subQ5=sQuery(id+"F0.wireOp",EDGE,"E1.bottom");var subQ6=sQuery(id+"F0.wireOp",EDGE,"E21.filletArc");var subQ7=sQuery(id+"F0.wireOp",EDGE,"E1.top");var subQ8=sQuery(id+"F0.wireOp",EDGE,"E1.left");var subQ9=sQuery(id+"F0.wireOp",EDGE,"E1.right");var subQ10=sQuery(id+"F0.wireOp",EDGE,"E23.filletArc");var subQ11=sQuery(id+"F0.wireOp",EDGE,"E24.filletArc");Q0=makeQuery(id+"F2.boolean.opBoolean","SPLIT",FACE,{"disambiguationData":[TD([makeQuery(id+"F1.opExtrude","SWEPT_FACE",FACE,{"disambiguationData":[OSD([subQ5])]})])],"derivedFrom":makeQuery(id+"F1.opExtrude","CAP_FACE",FACE,{"disambiguationData":[OSD([subQ5,subQ7,subQ8,subQ9,subQ4,subQ3,subQ2,subQ1,subQ6,subQ0,subQ10,subQ11])],"isStart":true})});}
            var sketch = newSketch(context, id + "F16", { "sketchPlane" : qUnion([Q0])});
            skLineSegment(sketch, "E79", {"start": v(0, 135) * mm, "end": v(0, 165) * mm, "construction": true});
            skCircle(sketch, "E80", {"center": v(0, 165) * mm, "radius": 6 * mm});
            skLineSegment(sketch, "E81", {"start": v(15, 164.51) * mm, "end": v(15.06, 153) * mm});
            skLineSegment(sketch, "E82", {"start": v(-15, 164.68) * mm, "end": v(-14.75, 153) * mm});
            skLineSegment(sketch, "E83", {"start": v(-14.75, 153) * mm, "end": v(-32.75, 135) * mm});
            skLineSegment(sketch, "E84", {"start": v(15.06, 153) * mm, "end": v(33.06, 135) * mm});
            skArc(sketch, "E85", {"start": v(-15, 164.68) * mm, "mid": v(0.08, 180) * mm, "end": v(15, 164.51) * mm});
            skLineSegment(sketch, "E86", {"start": v(-80, 0) * mm, "end": v(80, 0) * mm, "construction": true});
            skLineSegment(sketch, "E87.MirrorCS", {"start": v(-14.75, -153) * mm, "end": v(-32.75, -135) * mm});
            skLineSegment(sketch, "E88.MirrorCS", {"start": v(-15, -164.68) * mm, "end": v(-14.75, -153) * mm});
            skArc(sketch, "E89.MirrorCS", {"start": v(-15, -164.68) * mm, "mid": v(0.08, -180) * mm, "end": v(15, -164.51) * mm});
            skLineSegment(sketch, "E90.MirrorCS", {"start": v(15, -164.51) * mm, "end": v(15.06, -153) * mm});
            skLineSegment(sketch, "E91.MirrorCS", {"start": v(15.06, -153) * mm, "end": v(33.06, -135) * mm});
            skCircle(sketch, "E92.MirrorC", {"center": v(0, -165) * mm, "radius": 6 * mm});
            skLineSegment(sketch, "E93.MirrorCS", {"start": v(0, -135) * mm, "end": v(0, -165) * mm, "construction": true});
            skSolve(sketch);
        }
        {
            var Q0;
            {var subQ0=sQuery(id+"F16.wireOp",EDGE,"E87.MirrorCS");Q0=makeQuery(id+"F16.imprint","IMPRINT",FACE,{"disambiguationData":[TD([[makeQuery(id+"F16.imprint","IMPRINT",EDGE,{"derivedFrom":subQ0}),-1.0]])]});}
            var Q1;
            Q1=makeQuery(id+"F16.imprint","IMPRINT",FACE,{"disambiguationData":[TD([[makeQuery(id+"F16.imprint","IMPRINT",EDGE,{"derivedFrom":sQuery(id+"F16.wireOp",EDGE,"E80")}),-1.0]])]});
            var Q2;
            Q2=makeQuery(id+"F16.imprint","IMPRINT",FACE,{"disambiguationData":[TD([[makeQuery(id+"F16.imprint","IMPRINT",EDGE,{"derivedFrom":makeQuery(id+"F1.opExtrude","CAP_EDGE",EDGE,{"disambiguationData":[OSD([sQuery(id+"F0.wireOp",EDGE,"E1.left")])],"isStart":true})}),-1.0]])]});
            var Q3;
            Q3=makeQuery(id+"F2.opExtrude","CAP_FACE",FACE,{"disambiguationData":[OSD([sQuery(id+"F0.wireOp",EDGE,"E12"),sQuery(id+"F0.wireOp",EDGE,"E13"),sQuery(id+"F0.wireOp",EDGE,"E14"),sQuery(id+"F0.wireOp",EDGE,"E15"),sQuery(id+"F0.wireOp",EDGE,"E17.filletArc"),sQuery(id+"F0.wireOp",EDGE,"E18.filletArc"),sQuery(id+"F0.wireOp",EDGE,"E19.filletArc"),sQuery(id+"F0.wireOp",EDGE,"E20.filletArc"),sQuery(id+"F0.wireOp",EDGE,"E25.0"),sQuery(id+"F0.wireOp",EDGE,"E25.1"),sQuery(id+"F0.wireOp",EDGE,"E25.2"),sQuery(id+"F0.wireOp",EDGE,"E25.3"),sQuery(id+"F0.wireOp",EDGE,"E25.4"),sQuery(id+"F0.wireOp",EDGE,"E25.5"),sQuery(id+"F0.wireOp",EDGE,"E25.6"),sQuery(id+"F0.wireOp",EDGE,"E25.7")])],"isStart":false});
            extrude(context, id + "F17", {"entities" : qUnion([Q0, Q1, Q2]), "operationType" : NewBodyOperationType.ADD, "endBound" : BoundingType.UP_TO_SURFACE, "endBoundEntityFace" : qUnion([Q3]), "depth" : 25 * mm});
        }
    });
